# Revit family: LQ1020001_Grifería Para Lavamanos 8 Pulgadas Liquid
name_source: partatom
category: Plumbing Fixtures
units: mm (PartAtom-declared; Revit-internal decimal feet)

## family parameters
Always vertical = Yes
Cut with Voids When Loaded = No
OmniClass Number = 23.31.11.00
OmniClass Title = Faucets
Part Type = Normal
Room Calculation Point = No
Round Connector Dimension = Use Diameter
Shared = No
Work Plane-Based = No

## types (1)
- LQ1020001_Grifería Para Lavamanos 8 Pulgadas Liquid
    Acabado = Cromado
    Alto = 13.86 cm
    Altura de la grifería = Baja
    Ancho = 20.32 cm
    Capacidad de flujo = 5.70 l/m máximo a 60 psi
    Colección = Liquid
    Consumo de agua = 5.7 lt
    Creado por = IDD
    Description = La línea de griferías, duchas y accesorios Liquid se inspira en la tensión superficial del agua y en cómo esta crea formas armoniosas adaptándose al ambiente.
Las griferías Liquid juegan con la luz y los reflejos que fluyen alrededor de sus formas, sus líneas continuas y simplicidad. ¡Tu mejor opción!
    Fecha de creación = 31/07/2020
    Garantía = 30 años en estructura
    Garantías de otros componentes = 5 años en acabados
    Incluye = Cuerpo, Pico, Manijas, Acoples
    Largo = 17.47 cm
    Línea = Liquid
    Material = Corona_Metal
    Materiales = Metal
    Productos compatibles = Lavamanos de mesón integrado, Lavamanos para sobreponer, Lavamanos para incrustar
    Rango de presión de agua = Entre 20 y 125 psi
    Resistencia = Resistente a la corrosión pelado y decoloración por agua
    Sistema de accionamiento = Palanca
    Tecnologías = DuraCrome, EcoStream, ThermoControl
    Temperatura de uso = Entre 5˚C y 71˚C
    Tipo de chorro = Espumoso
    Tipo de grifería = 8 pulgadas
    Tipo de manija/accionamiento = Palanca
    URL = https://corona.co
    Uso = Residencial

## geometry (parser evidence)
native form markers: Sweep x5
no freeform markers — native parametric forms only
